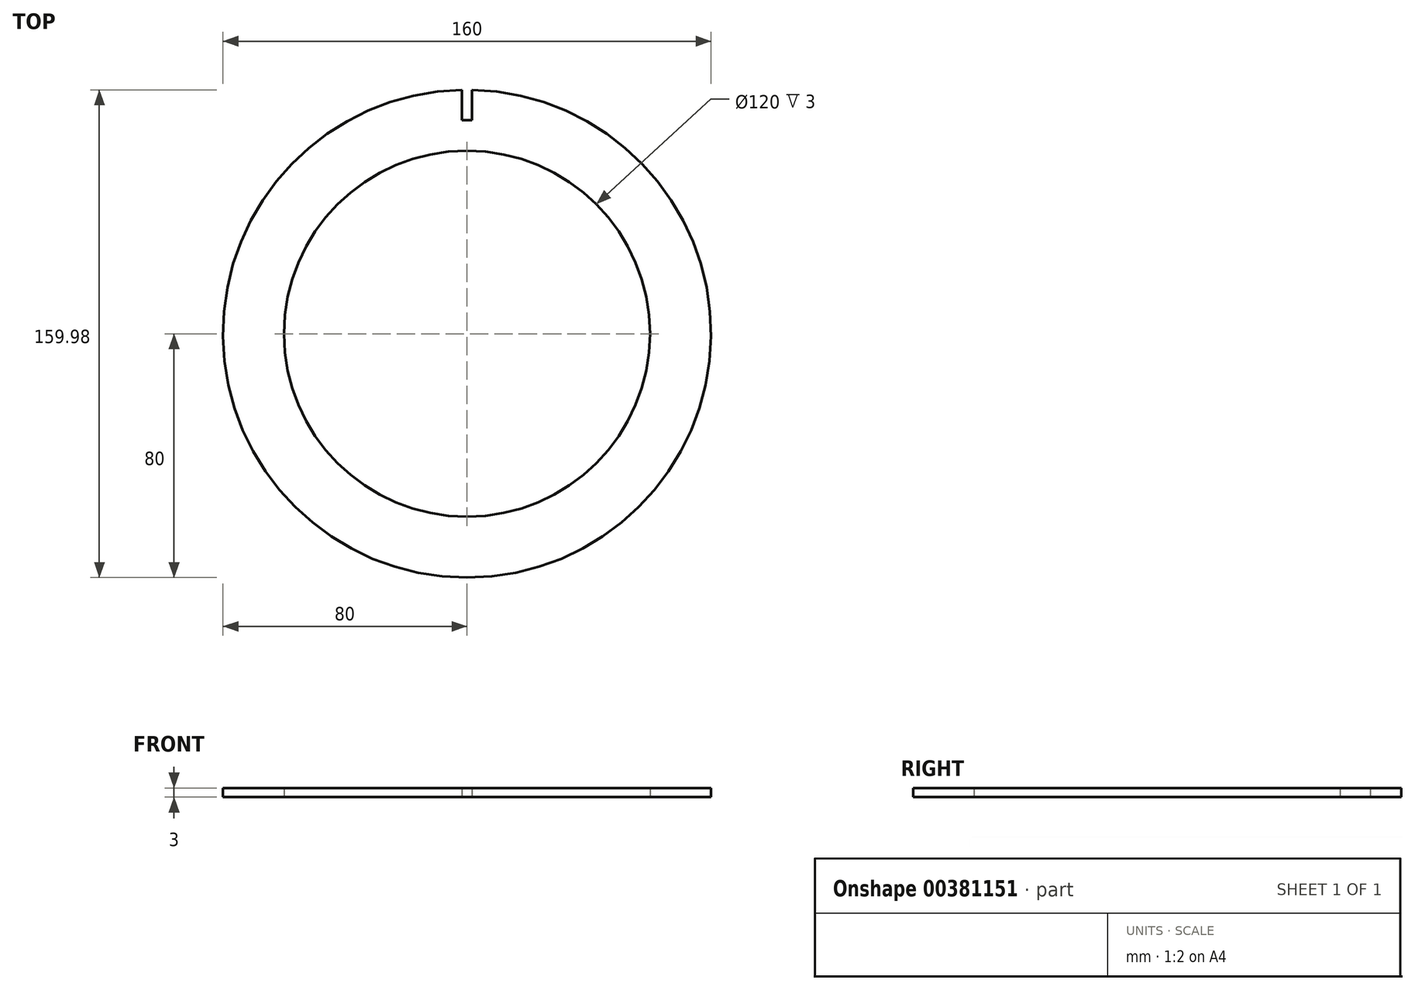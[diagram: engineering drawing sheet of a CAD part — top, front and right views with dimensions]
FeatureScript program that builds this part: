
annotation { "Feature Type Name" : "Feature", "Feature Type Description" : "" }
export const myFeature = defineFeature(function(context is Context, id is Id, definition is map)
    precondition{}
    {
        {
            var Q0;
            Q0=qCreatedBy(makeId("Top.planeOp"),FACE);
            var sketch = newSketch(context, id + "F0", { "sketchPlane" : qUnion([Q0])});
            skCircle(sketch, "E0", {"center": v(0, 0) * mm, "radius": 80 * mm});
            skCircle(sketch, "E1", {"center": v(0, 0) * mm, "radius": 60 * mm});
            skSolve(sketch);
        }
        {
            var Q0;
            Q0=makeQuery(id+"F0.imprint","IMPRINT",FACE,{"disambiguationData":[TD([[makeQuery(id+"F0.imprint","IMPRINT",EDGE,{"derivedFrom":sQuery(id+"F0.wireOp",EDGE,"E0")}),1.0]])]});
            extrude(context, id + "F1", {"entities" : qUnion([Q0]), "depth" : 3 * mm, "offsetDistance" : 25 * mm});
        }
        {
            var Q0;
            Q0=makeQuery(id+"F1.opExtrude","CAP_FACE",FACE,{"disambiguationData":[OSD([sQuery(id+"F0.wireOp",EDGE,"E0"),sQuery(id+"F0.wireOp",EDGE,"E1")])],"isStart":false});
            var sketch = newSketch(context, id + "F2", { "sketchPlane" : qUnion([Q0])});
            skLineSegment(sketch, "E2.bottom", {"start": v(-1.6, 80) * mm, "end": v(1.6, 80) * mm});
            skLineSegment(sketch, "E2.top", {"start": v(-1.6, 70) * mm, "end": v(1.6, 70) * mm});
            skLineSegment(sketch, "E2.left", {"start": v(-1.6, 80) * mm, "end": v(-1.6, 70) * mm});
            skLineSegment(sketch, "E2.right", {"start": v(1.6, 80) * mm, "end": v(1.6, 70) * mm});
            skLineSegment(sketch, "E3", {"start": v(0, 0) * mm, "end": v(0, 70) * mm, "construction": true});
            skSolve(sketch);
        }
        {
            var Q0;
            Q0 = qSketchRegion(id + "F2", true);
            extrude(context, id + "F3", {"entities" : qUnion([Q0]), "operationType" : NewBodyOperationType.REMOVE, "oppositeDirection" : true, "depth" : 25 * mm});
        }
    });
